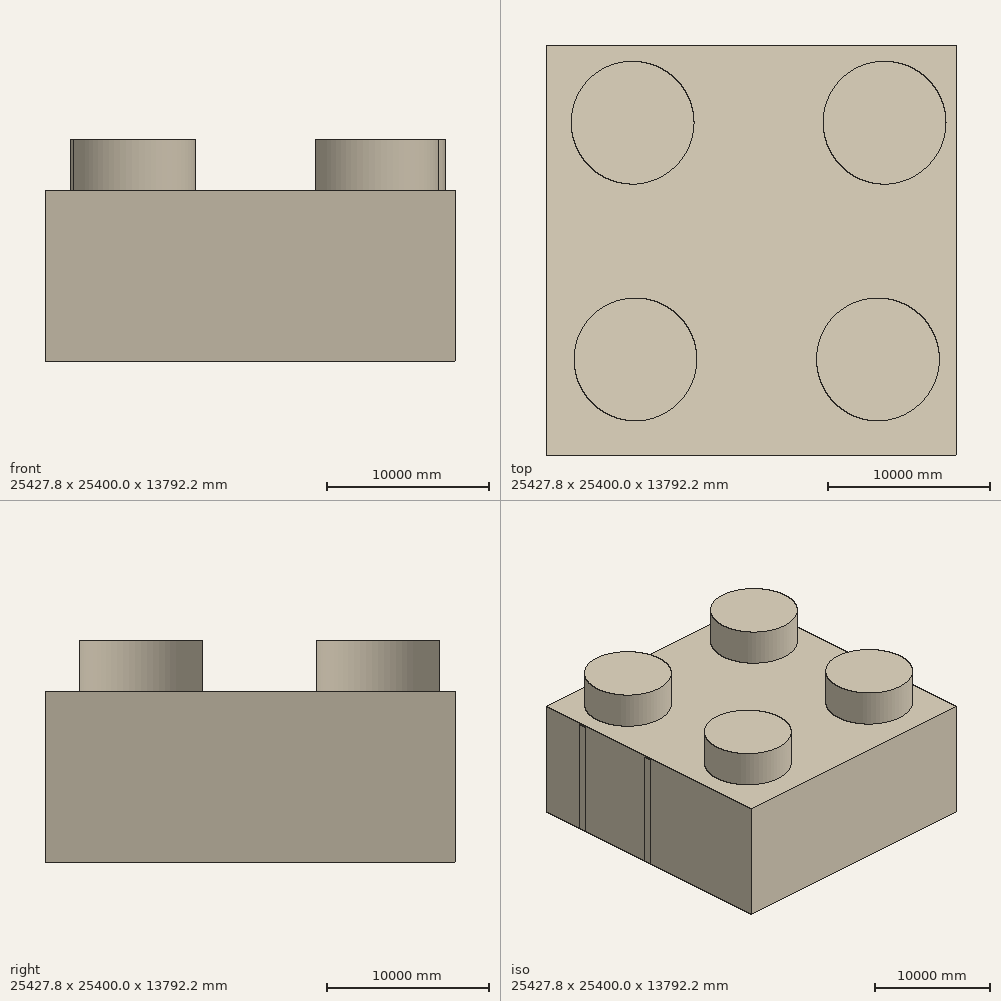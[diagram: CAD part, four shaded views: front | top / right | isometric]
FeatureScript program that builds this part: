
annotation { "Feature Type Name" : "Feature", "Feature Type Description" : "" }
export const myFeature = defineFeature(function(context is Context, id is Id, definition is map)
    precondition{}
    {
        {
            var Q0;
            Q0=qCreatedBy(makeId("Top.planeOp"),FACE);
            var sketch = newSketch(context, id + "F0", { "sketchPlane" : qUnion([Q0])});
            skLineSegment(sketch, "E0.bottom", {"start": v(-12705.46, 16623.6) * mm, "end": v(12694.54, 16623.6) * mm});
            skLineSegment(sketch, "E0.top", {"start": v(-12705.46, -8776.4) * mm, "end": v(12694.54, -8776.4) * mm});
            skLineSegment(sketch, "E0.left", {"start": v(-12705.46, 16623.6) * mm, "end": v(-12705.46, -8776.4) * mm});
            skLineSegment(sketch, "E0.right", {"start": v(12694.54, 16623.6) * mm, "end": v(12694.54, -8776.4) * mm});
            skLineSegment(sketch, "E1", {"start": v(12694.54, -2836.13) * mm, "end": v(12694.54, 11846.93) * mm});
            skLineSegment(sketch, "E2", {"start": v(-12705.46, 11846.93) * mm, "end": v(-12705.46, -2836.13) * mm});
            skCircle(sketch, "E3", {"center": v(-7391.13, 11846.93) * mm, "radius": 3810 * mm});
            skCircle(sketch, "E4", {"center": v(8235.42, 11846.93) * mm, "radius": 3810 * mm});
            skCircle(sketch, "E5", {"center": v(-7214.23, -2836.13) * mm, "radius": 3810 * mm});
            skCircle(sketch, "E6", {"center": v(7822.64, -2836.13) * mm, "radius": 3810 * mm});
            skSolve(sketch);
        }
        {
            var Q0;
            {var subQ1=sQuery(id+"F0.wireOp",EDGE,"E0.bottom");Q0=makeQuery(id+"F0.imprint","IMPRINT",FACE,{"disambiguationData":[TD([[makeQuery(id+"F0.imprint","IMPRINT",EDGE,{"derivedFrom":subQ1}),-1.0]])]});}
            extrude(context, id + "F1", {"entities" : qUnion([Q0]), "depth" : 10642.6 * mm});
        }
        {
            var Q0;
            Q0=makeQuery(id+"F0.imprint","IMPRINT",FACE,{"disambiguationData":[TD([[makeQuery(id+"F0.imprint","IMPRINT",EDGE,{"derivedFrom":sQuery(id+"F0.wireOp",EDGE,"E3")}),1.0]])]});
            var Q1;
            Q1=makeQuery(id+"F0.imprint","IMPRINT",FACE,{"disambiguationData":[TD([[makeQuery(id+"F0.imprint","IMPRINT",EDGE,{"derivedFrom":sQuery(id+"F0.wireOp",EDGE,"E4")}),1.0]])]});
            var Q2;
            Q2=makeQuery(id+"F0.imprint","IMPRINT",FACE,{"disambiguationData":[TD([[makeQuery(id+"F0.imprint","IMPRINT",EDGE,{"derivedFrom":sQuery(id+"F0.wireOp",EDGE,"E6")}),1.0]])]});
            var Q3;
            Q3=makeQuery(id+"F0.imprint","IMPRINT",FACE,{"disambiguationData":[TD([[makeQuery(id+"F0.imprint","IMPRINT",EDGE,{"derivedFrom":sQuery(id+"F0.wireOp",EDGE,"E5")}),1.0]])]});
            extrude(context, id + "F2", {"entities" : qUnion([Q0, Q1, Q2, Q3]), "operationType" : NewBodyOperationType.ADD, "depth" : 13792.2 * mm});
        }
        {
            var Q0;
            {var subQ0=sQuery(id+"F0.wireOp",EDGE,"E6");var subQ1=sQuery(id+"F0.wireOp",EDGE,"E5");var subQ2=sQuery(id+"F0.wireOp",EDGE,"E4");var subQ3=sQuery(id+"F0.wireOp",EDGE,"E3");Q0=makeQuery(id+"F2.boolean.opBoolean","MERGE",FACE,{"derivedFrom":[makeQuery(id+"F1.opExtrude","CAP_FACE",FACE,{"disambiguationData":[OSD([sQuery(id+"F0.wireOp",EDGE,"E0.bottom"),sQuery(id+"F0.wireOp",EDGE,"E0.top"),sQuery(id+"F0.wireOp",EDGE,"E0.left"),sQuery(id+"F0.wireOp",EDGE,"E0.right"),sQuery(id+"F0.wireOp",EDGE,"E1"),sQuery(id+"F0.wireOp",EDGE,"E2"),subQ3,subQ2,subQ1,subQ0])],"isStart":true}),makeQuery(id+"F2.opExtrude","CAP_FACE",FACE,{"disambiguationData":[OSD([subQ3])],"isStart":true}),makeQuery(id+"F2.opExtrude","CAP_FACE",FACE,{"disambiguationData":[OSD([subQ2])],"isStart":true}),makeQuery(id+"F2.opExtrude","CAP_FACE",FACE,{"disambiguationData":[OSD([subQ1])],"isStart":true}),makeQuery(id+"F2.opExtrude","CAP_FACE",FACE,{"disambiguationData":[OSD([subQ0])],"isStart":true})]});}
            shell(context, id + "F3", {"entities" : qUnion([Q0]), "thickness" : 2.54 * mm});
        }
        {
            var Q0;
            {var subQ1=sQuery(id+"F0.wireOp",EDGE,"E0.bottom");Q0=makeQuery(id+"F0.imprint","IMPRINT",FACE,{"disambiguationData":[TD([[makeQuery(id+"F0.imprint","IMPRINT",EDGE,{"derivedFrom":subQ1}),-1.0]])]});}
            var sketch = newSketch(context, id + "F4", { "sketchPlane" : qUnion([Q0])});
            skLineSegment(sketch, "E7.bottom", {"start": v(-12684.64, -4213.42) * mm, "end": v(12625.14, -4213.42) * mm});
            skLineSegment(sketch, "E7.top", {"start": v(-12684.64, -3533.3) * mm, "end": v(12625.14, -3533.3) * mm});
            skLineSegment(sketch, "E7.left", {"start": v(-12684.64, -4213.42) * mm, "end": v(-12684.64, -3533.3) * mm});
            skLineSegment(sketch, "E7.right", {"start": v(12625.14, -4213.42) * mm, "end": v(12625.14, -3533.3) * mm});
            skLineSegment(sketch, "E8.bottom", {"start": v(-12733.22, 3753.58) * mm, "end": v(12625.14, 3753.58) * mm});
            skLineSegment(sketch, "E8.top", {"start": v(-12733.22, 4482.26) * mm, "end": v(12625.14, 4482.26) * mm});
            skLineSegment(sketch, "E8.left", {"start": v(-12733.22, 3753.58) * mm, "end": v(-12733.22, 4482.26) * mm});
            skLineSegment(sketch, "E8.right", {"start": v(12625.14, 3753.58) * mm, "end": v(12625.14, 4482.26) * mm});
            skLineSegment(sketch, "E9.bottom", {"start": v(12625.14, 11817.73) * mm, "end": v(-12733.22, 11817.73) * mm});
            skLineSegment(sketch, "E9.top", {"start": v(12625.14, 12497.84) * mm, "end": v(-12733.22, 12497.84) * mm});
            skLineSegment(sketch, "E9.left", {"start": v(12625.14, 11817.73) * mm, "end": v(12625.14, 12497.84) * mm});
            skLineSegment(sketch, "E9.right", {"start": v(-12733.22, 11817.73) * mm, "end": v(-12733.22, 12497.84) * mm});
            skSolve(sketch);
        }
        {
            var Q0;
            Q0 = qSketchRegion(id + "F4", true);
            extrude(context, id + "F5", {"entities" : qUnion([Q0]), "operationType" : NewBodyOperationType.ADD, "depth" : 10515.6 * mm});
        }
    });
